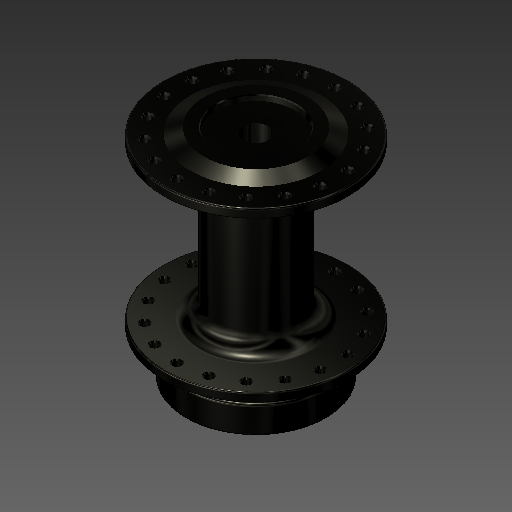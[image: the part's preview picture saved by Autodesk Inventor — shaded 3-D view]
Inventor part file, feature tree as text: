
AUTODESK INVENTOR PART (.ipt)
format: ipt  version: 2018 (Build 220112000, 112)  size: 504,320 bytes
history: native  units: mm
features: chamfer x6, fillet x5, sketch x5, extrude x4, pattern_circular x2, revolve x1, hole x1
ambient origin geometry x8: Origin, YZ Plane, XZ Plane, XY Plane, X Axis, Y Axis, Z Axis, Center Point
bodies: Body1 (feature_tree)
feature tree (24):
  revolve  "Revolution1"  [1 undecoded]
  chamfer  "Chamfer1"  Distance=3.42mm
  fillet  "Fillet1"  Radius=6.0mm
  extrude  "Extrusion2"  Depth=2.0mm
  chamfer  "Chamfer2"  Distance=19.58mm
  pattern_circular  "Circular Pattern1"  [2 undecoded]
  extrude  "Extrusion3"  TaperAngle=90.0deg  [1 undecoded]
  chamfer  "Chamfer3"  Distance=10.0mm Angle=45.0deg
  pattern_circular  "Circular Pattern2"  [2 undecoded]
  extrude  "Extrusion4"  Depth=2.0mm
  chamfer  "Chamfer4"  Distance=5.0mm
  fillet  "Fillet2"  [1 undecoded]
  fillet  "Fillet3"  Radius=2.0mm
  fillet  "Fillet4"  Radius=180.0mm
  fillet  "Fillet5"  Radius=4.01mm
  extrude  "Extrusion5"  Depth=2.0mm
  hole  "Hole1"  [1 undecoded]
  chamfer  "Chamfer5"  Distance=2.0mm Angle=45.0deg
  chamfer  "Chamfer6"  Distance=60.0mm Angle=360.0deg
  sketch  "Sketch1"  dims[d3=15.0mm d4=55.0mm]
  sketch  "Sketch4"  dims[d5=34.0mm]
  sketch  "Sketch5"  dims[d6=34.0mm]
  sketch  "Sketch6"  dims[d7=21.5mm]
  sketch  "Sketch7"  dims[d8=3.42mm d9=3.42mm d10=6.0mm d11=26.0mm d12=19.58mm d13=17.5mm d14=90.0deg d15=10.0mm d16=2.0mm d17=45.0deg d18=4.0mm d19=2.7mm d21=5.0mm d22=0.0mm d23=0.0mm d24=0.5mm d25=2.0mm d26=45.0deg d27=180.0mm d28=360.0deg d30=4.01mm d31=4.0mm d32=10.0mm d33=0.0mm d34=0.5mm d35=2.0mm d36=45.0deg d37=60.0mm d38=360.0deg d40=38.0mm d41=29.0mm d42=2.0mm d43=0.0mm d44=5.0mm d45=2.0mm d46=3.804818mm d47=6.0mm d48=2.0mm d49=1.0mm d50=0.6mm d51=32.8mm d52=29.0mm d53=2.0mm d54=0.0mm d55=10.0mm d56=10.0mm d57=9.02mm d58=6.0mm d59=4.0mm d60=2.0mm d61=90.0deg d62=8.0mm d63=20.594885mm d64=0.3mm d65=2.0mm d66=45.0deg d67=0.3mm d68=2.0mm d69=45.0deg]
note: 8 required parameter values undecoded (feature->parameter linkage not recoverable at this tier; creation-order binding heuristic only, values carry confidence <= 0.55)